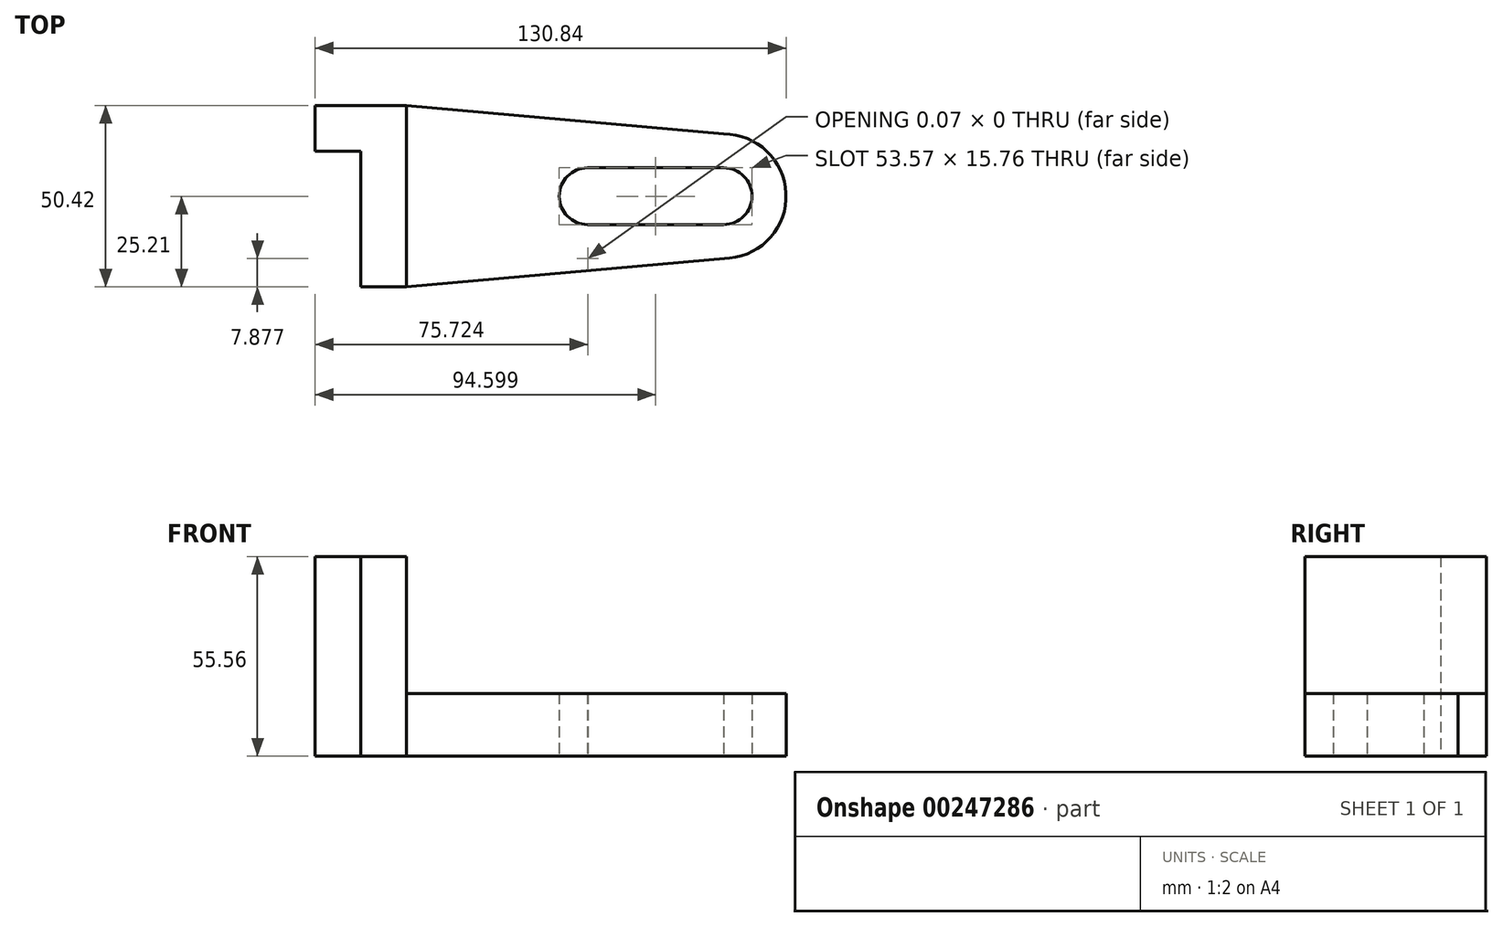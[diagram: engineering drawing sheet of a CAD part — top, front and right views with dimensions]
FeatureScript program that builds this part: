
annotation { "Feature Type Name" : "Feature", "Feature Type Description" : "" }
export const myFeature = defineFeature(function(context is Context, id is Id, definition is map)
    precondition{}
    {
        {
            var Q0;
            Q0=qCreatedBy(makeId("Top.planeOp"),FACE);
            var sketch = newSketch(context, id + "F0", { "sketchPlane" : qUnion([Q0])});
            skArc(sketch, "E0", {"start": v(0, 7.88) * mm, "mid": v(-5.57, 5.57) * mm, "end": v(-7.88, 0) * mm});
            skArc(sketch, "E1", {"start": v(45.7, 0) * mm, "mid": v(43.39, 5.57) * mm, "end": v(37.82, 7.88) * mm});
            skArc(sketch, "E2", {"start": v(0, 17.33) * mm, "mid": v(-12.26, 12.26) * mm, "end": v(-17.33, 0) * mm});
            skArc(sketch, "E3", {"start": v(39.44, -17.26) * mm, "mid": v(55.13, 0.81) * mm, "end": v(37.82, 17.33) * mm});
            skLineSegment(sketch, "E4", {"start": v(0, 17.33) * mm, "end": v(37.82, 17.33) * mm});
            skLineSegment(sketch, "E5", {"start": v(0, -17.33) * mm, "end": v(0.07, -17.33) * mm});
            skLineSegment(sketch, "E6", {"start": v(0, 7.88) * mm, "end": v(37.82, 7.88) * mm});
            skLineSegment(sketch, "E7", {"start": v(-63, 0) * mm, "end": v(-63, -25.21) * mm});
            skLineSegment(sketch, "E8", {"start": v(-63, 0) * mm, "end": v(-63, 12.51) * mm});
            skLineSegment(sketch, "E9", {"start": v(-63, 25.21) * mm, "end": v(-75.7, 25.21) * mm});
            skLineSegment(sketch, "E10", {"start": v(-75.7, 25.21) * mm, "end": v(-75.7, 12.51) * mm});
            skLineSegment(sketch, "E11", {"start": v(-75.7, 12.51) * mm, "end": v(-63, 12.51) * mm});
            skLineSegment(sketch, "E12", {"start": v(-63, 25.21) * mm, "end": v(-50.3, 25.21) * mm});
            skLineSegment(sketch, "E13", {"start": v(-50.3, 25.21) * mm, "end": v(-50.3, -25.21) * mm});
            skLineSegment(sketch, "E14", {"start": v(-50.3, -25.21) * mm, "end": v(-63, -25.21) * mm});
            skLineSegment(sketch, "E15", {"start": v(37.82, 17.33) * mm, "end": v(-50.3, 25.21) * mm});
            skLineSegment(sketch, "E16", {"start": v(-50.3, -25.21) * mm, "end": v(39.44, -17.26) * mm});
            skPoint(sketch, "E17.endSnap0", {"position": v(55.13, 0.81) * mm});
            skPoint(sketch, "E18.endSnap0", {"position": v(-7.88, 0) * mm});
            skPoint(sketch, "E19.start.orphan", {"position": v(0, -7.88) * mm});
            skArc(sketch, "E20.trimOffspring", {"start": v(0, -17.33) * mm, "mid": v(0.03, -17.33) * mm, "end": v(0.07, -17.33) * mm});
            skLineSegment(sketch, "E21.MirrorCS", {"start": v(0, -17.33) * mm, "end": v(37.82, -17.33) * mm});
            skArc(sketch, "E22.MirrorCS", {"start": v(0, -17.33) * mm, "mid": v(-12.26, -12.26) * mm, "end": v(-17.33, 0) * mm});
            skLineSegment(sketch, "E23.MirrorCS", {"start": v(0, -7.88) * mm, "end": v(37.82, -7.88) * mm});
            skArc(sketch, "E24.MirrorCS", {"start": v(45.7, 0) * mm, "mid": v(43.39, -5.57) * mm, "end": v(37.82, -7.88) * mm});
            skArc(sketch, "E25.MirrorCS", {"start": v(0, -7.88) * mm, "mid": v(-5.57, -5.57) * mm, "end": v(-7.88, 0) * mm});
            skPoint(sketch, "E26.MirrorCS.end.orphan", {"position": v(37.82, -17.33) * mm});
            skPoint(sketch, "E26.MirrorCS.start.orphan", {"position": v(37.82, -7.88) * mm});
            skPoint(sketch, "E27.orphan", {"position": v(55.13, 0) * mm});
            skSolve(sketch);
        }
        {
            var Q0;
            Q0=makeQuery(id+"F0.imprint","IMPRINT",FACE,{"disambiguationData":[TD([[makeQuery(id+"F0.imprint","IMPRINT",EDGE,{"derivedFrom":sQuery(id+"F0.wireOp",EDGE,"E0")}),-1.0]])]});
            extrude(context, id + "F1", {"entities" : qUnion([Q0]), "depth" : 17.46 * mm});
        }
        {
            var Q0;
            Q0=makeQuery(id+"F0.imprint","IMPRINT",FACE,{"disambiguationData":[TD([[makeQuery(id+"F0.imprint","IMPRINT",EDGE,{"derivedFrom":sQuery(id+"F0.wireOp",EDGE,"E7")}),1.0]])]});
            extrude(context, id + "F2", {"entities" : qUnion([Q0]), "depth" : 55.56 * mm});
        }
    });
